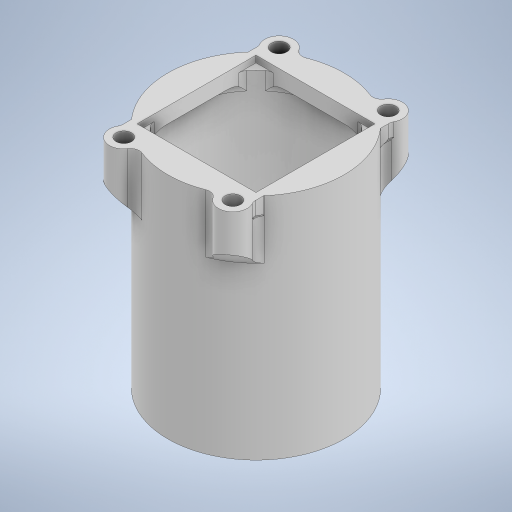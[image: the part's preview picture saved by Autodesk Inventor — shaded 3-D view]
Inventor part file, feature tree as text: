
AUTODESK INVENTOR PART (.ipt)
format: ipt  version: 2024 (Build 280153000, 153)  size: 545,280 bytes
history: native  units: in
note: dims shown in document units (in); Inventor stores cm internally (conversion verified against a paired STEP export)
features: extrude x9, projected_geometry x6, sketch x5, fillet x4, chamfer x1
ambient origin geometry x8: Origin, YZ Plane, XZ Plane, XY Plane, X Axis, Y Axis, Z Axis, Center Point
bodies: Solid1 (feature_tree)
feature tree (25):
  extrude  "Extrusion1"  Depth=1.5748in
  extrude  "Extrusion2"  Depth=0.9843in
  extrude  "Extrusion3"  Depth=0.1181in
  sketch  "Sketch4"  dims[d8=1.7106in d9=0.0in d10=0.1378in]
  extrude  "Extrusion4"  Depth=0.1378in
  extrude  "Extrusion5"  Depth=0.0787in
  extrude  "Extrusion6"  Depth=0.0787in
  extrude  "Extrusion7"  Depth=0.0787in
  extrude  "Extrusion8"  Depth=0.0787in
  fillet  "Fillet1"  Radius=0.2559in
  extrude  "Extrusion9"  Depth=0.0787in
  chamfer  "Chamfer1"  Distance=0.5906in
  fillet  "Fillet4"  Radius=0.5906in
  fillet  "Fillet5"  Radius=0.2362in
  fillet  "Fillet6"  Radius=0.2362in
  sketch  "Sketch1"  dims[d0=0.8386in d1=1.5748in]
  sketch  "Sketch2"  dims[d2=0.1181in d3=0.0in d4=0.9843in]
  sketch  "Sketch3"  dims[d5=0.1575in d6=0.0in d7=0.1181in]
  projected_geometry  "Projected Loop1"
  projected_geometry  "Projected Loop2"
  sketch  "Sketch5"  dims[d14=1.3878in d15=0.9744in d17=0.9744in d18=0.4872in d19=0.6939in d20=0.2559in d21=1.1811in d22=0.5906in d23=0.5906in d25=0.2362in d26=0.0in d27=0.2362in d28=0.0in d29=0.0591in d30=1.3878in d31=0.0787in d32=0.0in d33=0.0591in d34=0.0in d35=0.0591in d36=0.0in d37=0.0787in d39=0.0394in d40=0.0in d42=0.187in d43=0.0787in d44=45.0deg d45=0.0197in d46=0.0787in d47=0.0787in d41=0.0in d48=0.0197in d49=0.0344in d50=0.0197in d51=0.0344in]
  projected_geometry  "Projected Loop3"
  projected_geometry  "Projected Loop4"
  projected_geometry  "Projected Loop5"
  projected_geometry  "Projected Loop6"
